# Revit family: QF_T&S_B-3950
name_source: partatom
category: Specialty Equipment
revit_build: Autodesk Revit Architecture 2012 (Build: 20110916_2132(x64)
units: mm (PartAtom-declared; Revit-internal decimal feet)

## types (1)
- QF_T&S_B-3950
    Description = Rotary Waste Valve for 3 1/2” Sink Opening with Rough Chrome Plated Body, 2” NPT Male Outlet / 1 1/2” NPT Female Outlet, Twist Handle with Heat Resistant Plastic Grip, 2” NPT Female X 1 1/2” NPT Male Adapter, 3 1/2” Snap-In Removable Strainer and Overflow Outlet with Cap
    Faucet Material = QF_Metal-Stainless-Polished
    Indirect Waste Connection Height = 0"
    Indirect Waste Flow = 17.14 GPM
    Indirect Waste Size = 2"
    Manufacturer = T&S Brass and Bronze Works, Inc.
    Model = B-3950
    Plumbing Remarks = Discharge rate: 17.14 GPM max
    Product Documentation Link = http://catalog.tsbrass.com
    URL = http://www.tsbrass.com
    Waste Water Discharge Temperature = -460 °F
    Weight in Pounds = 0

## geometry (parser evidence)
native form markers: Blend x10, Sweep x2
no freeform markers — native parametric forms only
